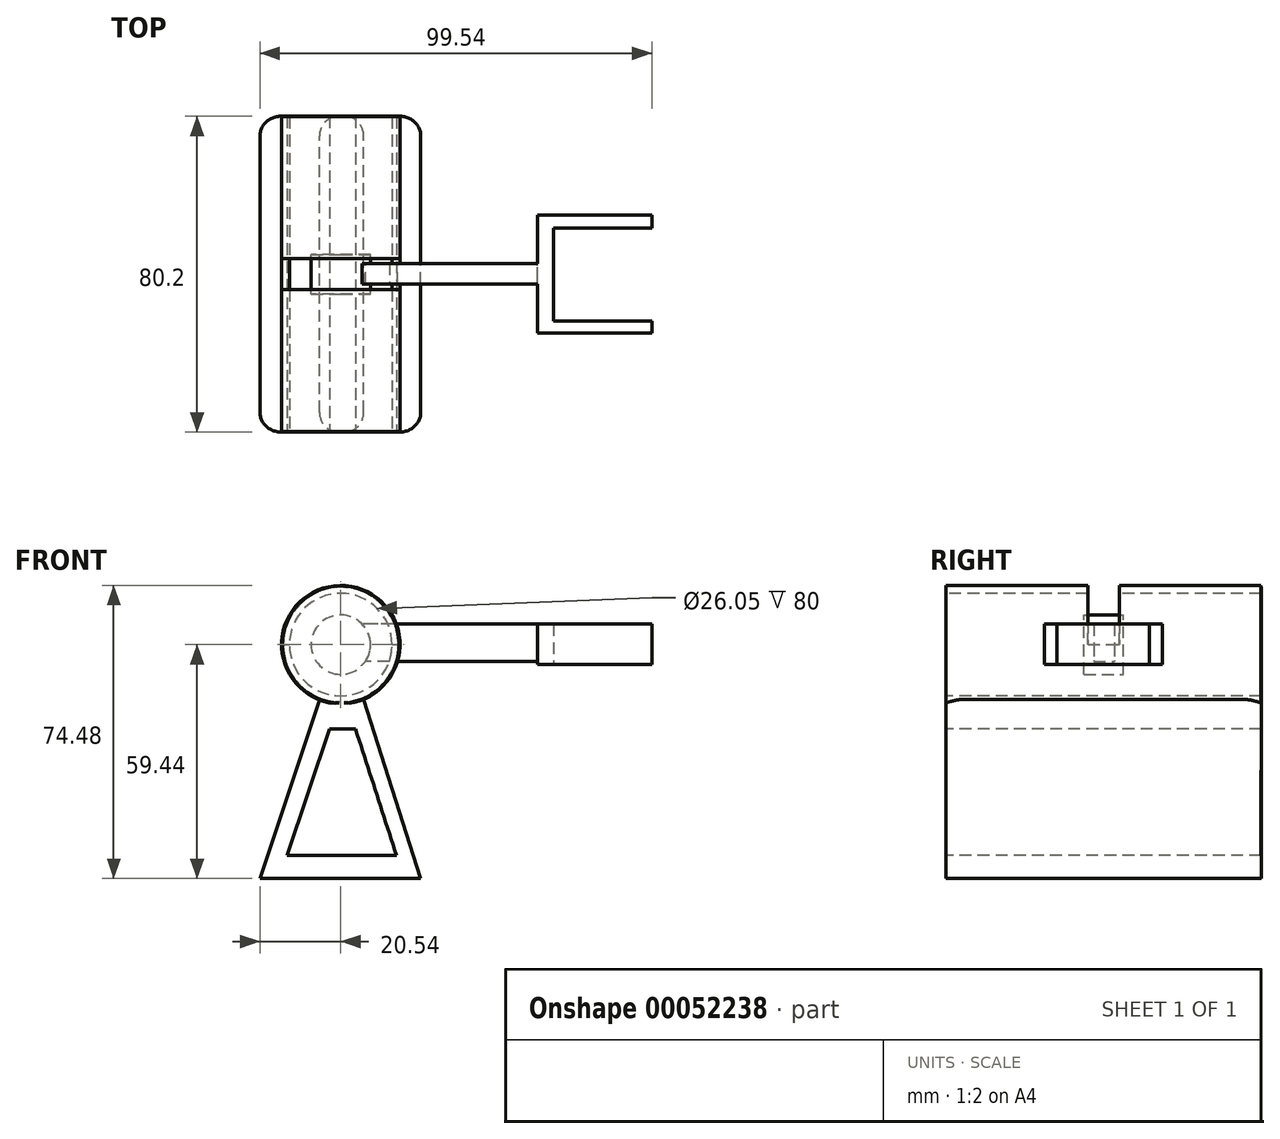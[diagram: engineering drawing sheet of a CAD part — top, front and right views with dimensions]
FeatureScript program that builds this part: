
annotation { "Feature Type Name" : "Feature", "Feature Type Description" : "" }
export const myFeature = defineFeature(function(context is Context, id is Id, definition is map)
    precondition{}
    {
        {
            var Q0;
            Q0=qCreatedBy(makeId("Front.planeOp"),FACE);
            var sketch = newSketch(context, id + "F0", { "sketchPlane" : qUnion([Q0])});
            skCircle(sketch, "E0", {"center": v(0, 0) * mm, "radius": 15.04 * mm});
            skSolve(sketch);
        }
        {
            var Q0;
            Q0 = qSketchRegion(id + "F0", true);
            extrude(context, id + "F1", {"entities" : qUnion([Q0]), "endBound" : BoundingType.SYMMETRIC, "depth" : 80 * mm});
        }
        {
            var Q0;
            Q0=makeQuery(id+"F1.opExtrude","CAP_FACE",FACE,{"disambiguationData":[OSD([sQuery(id+"F0.wireOp",EDGE,"E0")])],"isStart":false});
            var sketch = newSketch(context, id + "F2", { "sketchPlane" : qUnion([Q0])});
            skCircle(sketch, "E1", {"center": v(0, 0) * mm, "radius": 13.03 * mm});
            skSolve(sketch);
        }
        {
            var Q0;
            Q0 = qSketchRegion(id + "F2", true);
            extrude(context, id + "F3", {"entities" : qUnion([Q0]), "operationType" : NewBodyOperationType.REMOVE, "oppositeDirection" : true, "depth" : 80 * mm});
        }
        {
            var Q0;
            Q0=qCreatedBy(makeId("Right.planeOp"),FACE);
            var sketch = newSketch(context, id + "F4", { "sketchPlane" : qUnion([Q0])});
            skLineSegment(sketch, "E2.bottom", {"start": v(-3.97, 15.65) * mm, "end": v(3.97, 15.65) * mm});
            skLineSegment(sketch, "E2.top", {"start": v(-3.97, 0) * mm, "end": v(3.97, 0) * mm});
            skLineSegment(sketch, "E2.left", {"start": v(-3.97, 15.65) * mm, "end": v(-3.97, 0) * mm});
            skLineSegment(sketch, "E2.right", {"start": v(3.97, 15.65) * mm, "end": v(3.97, 0) * mm});
            skSolve(sketch);
        }
        {
            var Q0;
            Q0 = qSketchRegion(id + "F4", true);
            extrude(context, id + "F5", {"entities" : qUnion([Q0]), "operationType" : NewBodyOperationType.REMOVE, "endBound" : BoundingType.SYMMETRIC, "oppositeDirection" : true, "depth" : 35 * mm});
        }
        {
            var Q0;
            Q0=qCreatedBy(makeId("Front.planeOp"),FACE);
            var sketch = newSketch(context, id + "F6", { "sketchPlane" : qUnion([Q0])});
            skCircle(sketch, "E3", {"center": v(0, 0) * mm, "radius": 7.55 * mm});
            skSolve(sketch);
        }
        {
            var Q0;
            Q0 = qSketchRegion(id + "F6", true);
            extrude(context, id + "F7", {"entities" : qUnion([Q0]), "endBound" : BoundingType.SYMMETRIC, "depth" : 10 * mm});
        }
        {
            var Q0;
            Q0=qCreatedBy(makeId("Right.planeOp"),FACE);
            var sketch = newSketch(context, id + "F8", { "sketchPlane" : qUnion([Q0])});
            skLineSegment(sketch, "E4.bottom", {"start": v(-2.48, 5.21) * mm, "end": v(2.73, 5.21) * mm});
            skLineSegment(sketch, "E4.top", {"start": v(-2.48, -4.23) * mm, "end": v(2.73, -4.23) * mm});
            skLineSegment(sketch, "E4.left", {"start": v(-2.48, 5.21) * mm, "end": v(-2.48, -4.23) * mm});
            skLineSegment(sketch, "E4.right", {"start": v(2.73, 5.21) * mm, "end": v(2.73, -4.23) * mm});
            skSolve(sketch);
        }
        {
            var Q0;
            Q0 = qSketchRegion(id + "F8", true);
            extrude(context, id + "F9", {"entities" : qUnion([Q0]), "operationType" : NewBodyOperationType.ADD, "depth" : 50 * mm});
        }
        {
            var Q0;
            Q0=makeQuery(id+"F9.opExtrude","CAP_FACE",FACE,{"disambiguationData":[OSD([sQuery(id+"F8.wireOp",EDGE,"E4.bottom"),sQuery(id+"F8.wireOp",EDGE,"E4.top"),sQuery(id+"F8.wireOp",EDGE,"E4.left"),sQuery(id+"F8.wireOp",EDGE,"E4.right")])],"isStart":false});
            var sketch = newSketch(context, id + "F10", { "sketchPlane" : qUnion([Q0])});
            skLineSegment(sketch, "E5.bottom", {"start": v(-15, 5.21) * mm, "end": v(15, 5.21) * mm});
            skLineSegment(sketch, "E5.top", {"start": v(-15, -5) * mm, "end": v(15, -5) * mm});
            skLineSegment(sketch, "E5.left", {"start": v(-15, 5.21) * mm, "end": v(-15, -5) * mm});
            skLineSegment(sketch, "E5.right", {"start": v(15, 5.21) * mm, "end": v(15, -5) * mm});
            skSolve(sketch);
        }
        {
            var Q0;
            Q0 = qSketchRegion(id + "F10", true);
            extrude(context, id + "F11", {"entities" : qUnion([Q0]), "operationType" : NewBodyOperationType.ADD, "depth" : 4 * mm});
        }
        {
            var Q0;
            Q0=makeQuery(id+"F11.opExtrude","CAP_FACE",FACE,{"disambiguationData":[OSD([sQuery(id+"F10.wireOp",EDGE,"E5.bottom"),sQuery(id+"F10.wireOp",EDGE,"E5.top"),sQuery(id+"F10.wireOp",EDGE,"E5.left"),sQuery(id+"F10.wireOp",EDGE,"E5.right")])],"isStart":false});
            var sketch = newSketch(context, id + "F12", { "sketchPlane" : qUnion([Q0])});
            skLineSegment(sketch, "E6.bottom", {"start": v(-15, 5.21) * mm, "end": v(-11.87, 5.21) * mm});
            skLineSegment(sketch, "E6.top", {"start": v(-15, -5) * mm, "end": v(-11.87, -5) * mm});
            skLineSegment(sketch, "E6.left", {"start": v(-15, 5.21) * mm, "end": v(-15, -5) * mm});
            skLineSegment(sketch, "E6.right", {"start": v(-11.87, 5.21) * mm, "end": v(-11.87, -5) * mm});
            skSolve(sketch);
        }
        {
            var Q0;
            Q0 = qSketchRegion(id + "F12", true);
            extrude(context, id + "F13", {"entities" : qUnion([Q0]), "operationType" : NewBodyOperationType.ADD, "depth" : 25 * mm});
        }
        {
            var Q0;
            Q0=makeQuery(id+"F11.opExtrude","CAP_FACE",FACE,{"disambiguationData":[OSD([sQuery(id+"F10.wireOp",EDGE,"E5.bottom"),sQuery(id+"F10.wireOp",EDGE,"E5.top"),sQuery(id+"F10.wireOp",EDGE,"E5.left"),sQuery(id+"F10.wireOp",EDGE,"E5.right")])],"isStart":false});
            var sketch = newSketch(context, id + "F14", { "sketchPlane" : qUnion([Q0])});
            skLineSegment(sketch, "E7.bottom", {"start": v(11.68, 5.21) * mm, "end": v(15, 5.21) * mm});
            skLineSegment(sketch, "E7.top", {"start": v(11.68, -5) * mm, "end": v(15, -5) * mm});
            skLineSegment(sketch, "E7.left", {"start": v(11.68, 5.21) * mm, "end": v(11.68, -5) * mm});
            skLineSegment(sketch, "E7.right", {"start": v(15, 5.21) * mm, "end": v(15, -5) * mm});
            skSolve(sketch);
        }
        {
            var Q0;
            Q0 = qSketchRegion(id + "F14", true);
            extrude(context, id + "F15", {"entities" : qUnion([Q0]), "operationType" : NewBodyOperationType.ADD, "depth" : 25 * mm});
        }
        {
            var Q0;
            Q0=makeQuery(id+"F1.opExtrude","CAP_FACE",FACE,{"disambiguationData":[OSD([sQuery(id+"F0.wireOp",EDGE,"E0")])],"isStart":false});
            var sketch = newSketch(context, id + "F16", { "sketchPlane" : qUnion([Q0])});
            skCircle(sketch, "E8", {"center": v(0, 0) * mm, "radius": 14.85 * mm});
            skSolve(sketch);
        }
        {
            var Q0;
            Q0 = qSketchRegion(id + "F16", true);
            extrude(context, id + "F17", {"entities" : qUnion([Q0]), "operationType" : NewBodyOperationType.ADD, "depth" : 0.1 * mm});
        }
        {
            var Q0;
            Q0=makeQuery(id+"F1.opExtrude","CAP_FACE",FACE,{"disambiguationData":[OSD([sQuery(id+"F0.wireOp",EDGE,"E0")])],"isStart":true});
            var sketch = newSketch(context, id + "F18", { "sketchPlane" : qUnion([Q0])});
            skCircle(sketch, "E9", {"center": v(0, 0) * mm, "radius": 14.61 * mm});
            skSolve(sketch);
        }
        {
            var Q0;
            Q0 = qSketchRegion(id + "F18", true);
            extrude(context, id + "F19", {"entities" : qUnion([Q0]), "operationType" : NewBodyOperationType.ADD, "depth" : .1 * mm});
        }
        {
            var Q0;
            Q0=makeQuery(id+"F19.opExtrude","CAP_FACE",FACE,{"disambiguationData":[OSD([sQuery(id+"F18.wireOp",EDGE,"E9")])],"isStart":false});
            var sketch = newSketch(context, id + "F20", { "sketchPlane" : qUnion([Q0])});
            skLineSegment(sketch, "E10", {"start": v(-5.67, -13.47) * mm, "end": v(-20.33, -59.44) * mm});
            skLineSegment(sketch, "E11", {"start": v(-20.33, -59.44) * mm, "end": v(20.54, -59.44) * mm});
            skLineSegment(sketch, "E12", {"start": v(20.54, -59.44) * mm, "end": v(5.27, -13.63) * mm});
            skLineSegment(sketch, "E13", {"start": v(-5.67, -13.47) * mm, "end": v(5.27, -13.63) * mm});
            skSolve(sketch);
        }
        {
            var Q0;
            Q0 = qSketchRegion(id + "F20", true);
            extrude(context, id + "F21", {"entities" : qUnion([Q0]), "operationType" : NewBodyOperationType.ADD, "oppositeDirection" : true, "depth" : 80.2 * mm});
        }
        {
            var Q0;
            Q0=makeQuery(id+"F21.boolean.opBoolean","MERGE",FACE,{"derivedFrom":[makeQuery(id+"F17.opExtrude","CAP_FACE",FACE,{"disambiguationData":[OSD([sQuery(id+"F16.wireOp",EDGE,"E8")])],"isStart":false}),makeQuery(id+"F21.opExtrude","CAP_FACE",FACE,{"disambiguationData":[OSD([sQuery(id+"F20.wireOp",EDGE,"E10"),sQuery(id+"F20.wireOp",EDGE,"E11"),sQuery(id+"F20.wireOp",EDGE,"E12"),sQuery(id+"F20.wireOp",EDGE,"E13")])],"isStart":false})]});
            var sketch = newSketch(context, id + "F22", { "sketchPlane" : qUnion([Q0])});
            skLineSegment(sketch, "E14", {"start": v(-13.6, -53.5) * mm, "end": v(-2.9, -21.4) * mm});
            skLineSegment(sketch, "E15", {"start": v(-2.9, -21.4) * mm, "end": v(3.73, -21.4) * mm});
            skLineSegment(sketch, "E16", {"start": v(3.73, -21.4) * mm, "end": v(14.13, -53.5) * mm});
            skLineSegment(sketch, "E17", {"start": v(14.13, -53.5) * mm, "end": v(-13.6, -53.5) * mm});
            skSolve(sketch);
        }
        {
            var Q0;
            Q0 = qSketchRegion(id + "F22", true);
            extrude(context, id + "F23", {"entities" : qUnion([Q0]), "operationType" : NewBodyOperationType.REMOVE, "endBound" : BoundingType.THROUGH_ALL, "oppositeDirection" : true, "depth" : 25 * mm});
        }
        {
            var Q0;
            Q0=makeQuery(id+"F21.opExtrude","CAP_EDGE",EDGE,{"disambiguationData":[OSD([sQuery(id+"F20.wireOp",EDGE,"E10")])],"isStart":true});
            var Q1;
            Q1=makeQuery(id+"F21.opExtrude","CAP_EDGE",EDGE,{"disambiguationData":[OSD([sQuery(id+"F20.wireOp",EDGE,"E12")])],"isStart":true});
            var Q2;
            Q2=makeQuery(id+"F21.opExtrude","CAP_EDGE",EDGE,{"disambiguationData":[OSD([sQuery(id+"F20.wireOp",EDGE,"E12")])],"isStart":false});
            var Q3;
            Q3=makeQuery(id+"F21.opExtrude","CAP_EDGE",EDGE,{"disambiguationData":[OSD([sQuery(id+"F20.wireOp",EDGE,"E10")])],"isStart":false});
            fillet(context, id + "F24", {"entities" : qUnion([Q0, Q1, Q2, Q3]), "radius" : 5 * mm, "tangentPropagation" : true, "allowEdgeOverflow" : false});
        }
    });
